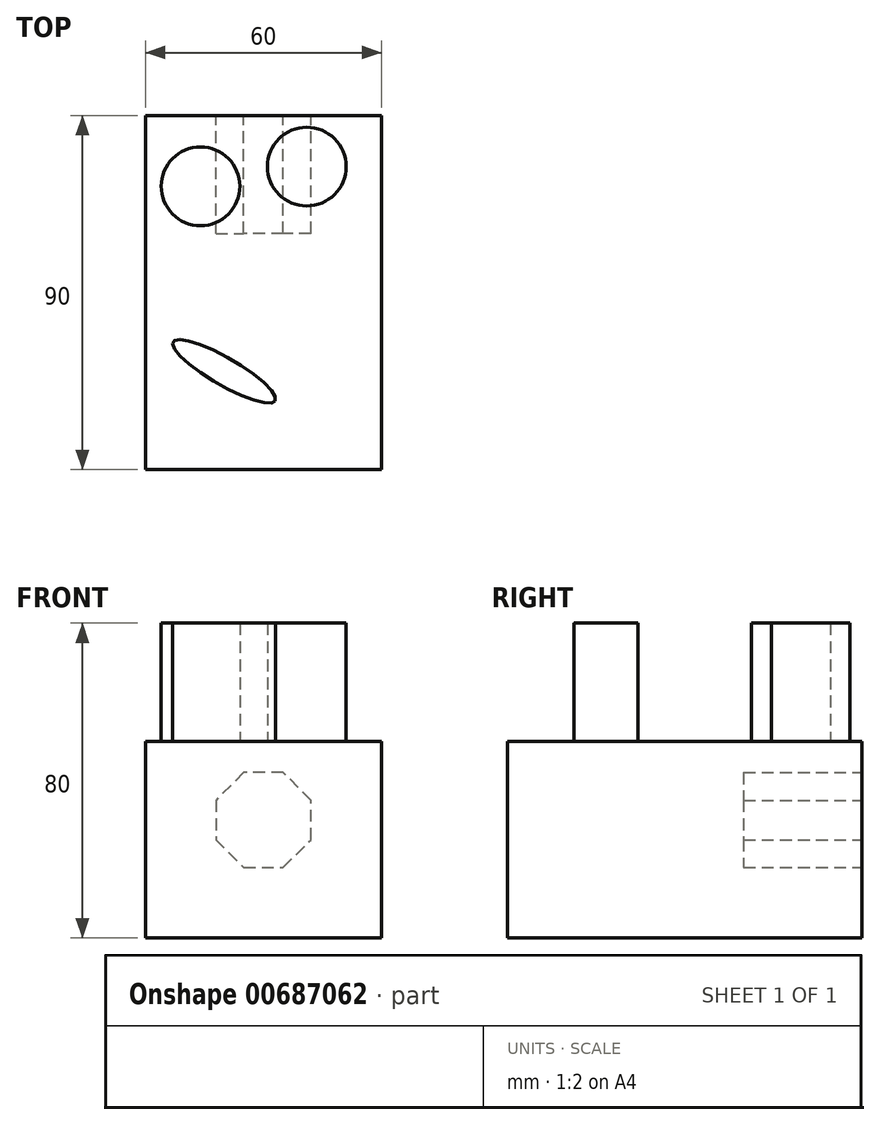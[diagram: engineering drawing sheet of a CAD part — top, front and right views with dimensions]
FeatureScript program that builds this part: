
annotation { "Feature Type Name" : "Feature", "Feature Type Description" : "" }
export const myFeature = defineFeature(function(context is Context, id is Id, definition is map)
    precondition{}
    {
        {
            var Q0;
            Q0=qCreatedBy(makeId("Top.planeOp"),FACE);
            var sketch = newSketch(context, id + "F0", { "sketchPlane" : qUnion([Q0])});
            skLineSegment(sketch, "E0.bottom", {"start": v(30, 45) * mm, "end": v(-30, 45) * mm});
            skLineSegment(sketch, "E0.top", {"start": v(30, -45) * mm, "end": v(-30, -45) * mm});
            skLineSegment(sketch, "E0.left", {"start": v(30, 45) * mm, "end": v(30, -45) * mm});
            skLineSegment(sketch, "E0.right", {"start": v(-30, 45) * mm, "end": v(-30, -45) * mm});
            skPoint(sketch, "E0.middle", {"position": v(0, 0) * mm});
            skSolve(sketch);
        }
        {
            var Q0;
            Q0 = qSketchRegion(id + "F0", true);
            extrude(context, id + "F1", {"entities" : qUnion([Q0]), "depth" : 50 * mm, "offsetDistance" : 25 * mm});
        }
        {
            var Q0;
            Q0=makeQuery(id+"F1.opExtrude","CAP_FACE",FACE,{"disambiguationData":[OSD([sQuery(id+"F0.wireOp",EDGE,"E0.bottom"),sQuery(id+"F0.wireOp",EDGE,"E0.top"),sQuery(id+"F0.wireOp",EDGE,"E0.left"),sQuery(id+"F0.wireOp",EDGE,"E0.right")])],"isStart":false});
            var sketch = newSketch(context, id + "F2", { "sketchPlane" : qUnion([Q0])});
            skCircle(sketch, "E1", {"center": v(-16, 27) * mm, "radius": 10 * mm});
            skCircle(sketch, "E2", {"center": v(11, 32) * mm, "radius": 10 * mm});
            skEllipse(sketch, "E3", {"center": v(-10, -20) * mm, "majorRadius": 15 * mm, "minorRadius": 3.5 * mm, "majorAxis": v(0.87, -0.5)});
            skLineSegment(sketch, "E4", {"start": v(-11.75, -23.03) * mm, "end": v(-8.25, -16.97) * mm, "construction": true});
            skSolve(sketch);
        }
        {
            var Q0;
            Q0=makeQuery(id+"F2.imprint","IMPRINT",FACE,{"disambiguationData":[TD([[makeQuery(id+"F2.imprint","IMPRINT",EDGE,{"derivedFrom":sQuery(id+"F2.wireOp",EDGE,"E2")}),1.0]])]});
            var Q1;
            Q1=makeQuery(id+"F2.imprint","IMPRINT",FACE,{"disambiguationData":[TD([[makeQuery(id+"F2.imprint","IMPRINT",EDGE,{"derivedFrom":sQuery(id+"F2.wireOp",EDGE,"E1")}),1.0]])]});
            var Q2;
            Q2=makeQuery(id+"F2.imprint","IMPRINT",FACE,{"disambiguationData":[TD([[makeQuery(id+"F2.imprint","IMPRINT",EDGE,{"derivedFrom":sQuery(id+"F2.wireOp",EDGE,"E3")}),1.0]])]});
            extrude(context, id + "F3", {"entities" : qUnion([Q0, Q1, Q2]), "operationType" : NewBodyOperationType.ADD, "depth" : 30 * mm, "offsetDistance" : 25 * mm});
        }
        {
            var Q0;
            Q0=makeQuery(id+"F1.opExtrude","SWEPT_FACE",FACE,{"disambiguationData":[OSD([sQuery(id+"F0.wireOp",EDGE,"E0.bottom")])]});
            var sketch = newSketch(context, id + "F4", { "sketchPlane" : qUnion([Q0])});
            skCircle(sketch, "E5.cCircle", {"center": v(0, 30) * mm, "radius": 12.07 * mm, "construction": true});
            skLineSegment(sketch, "E5.0", {"start": v(12.07, 25) * mm, "end": v(5, 17.93) * mm});
            skLineSegment(sketch, "E5.1", {"start": v(5, 17.93) * mm, "end": v(-5, 17.93) * mm});
            skLineSegment(sketch, "E5.2", {"start": v(-5, 17.93) * mm, "end": v(-12.07, 25) * mm});
            skLineSegment(sketch, "E5.3", {"start": v(-12.07, 25) * mm, "end": v(-12.07, 35) * mm});
            skLineSegment(sketch, "E5.4", {"start": v(-12.07, 35) * mm, "end": v(-5, 42.07) * mm});
            skLineSegment(sketch, "E5.5", {"start": v(-5, 42.07) * mm, "end": v(5, 42.07) * mm});
            skLineSegment(sketch, "E5.6", {"start": v(5, 42.07) * mm, "end": v(12.07, 35) * mm});
            skLineSegment(sketch, "E5.7", {"start": v(12.07, 35) * mm, "end": v(12.07, 25) * mm});
            skPoint(sketch, "E5.0.midPoint", {"position": v(8.54, 21.46) * mm});
            skSolve(sketch);
        }
        {
            var Q0;
            Q0 = qSketchRegion(id + "F4", true);
            extrude(context, id + "F5", {"entities" : qUnion([Q0]), "operationType" : NewBodyOperationType.REMOVE, "oppositeDirection" : true, "depth" : 30 * mm, "offsetDistance" : 25 * mm});
        }
    });
